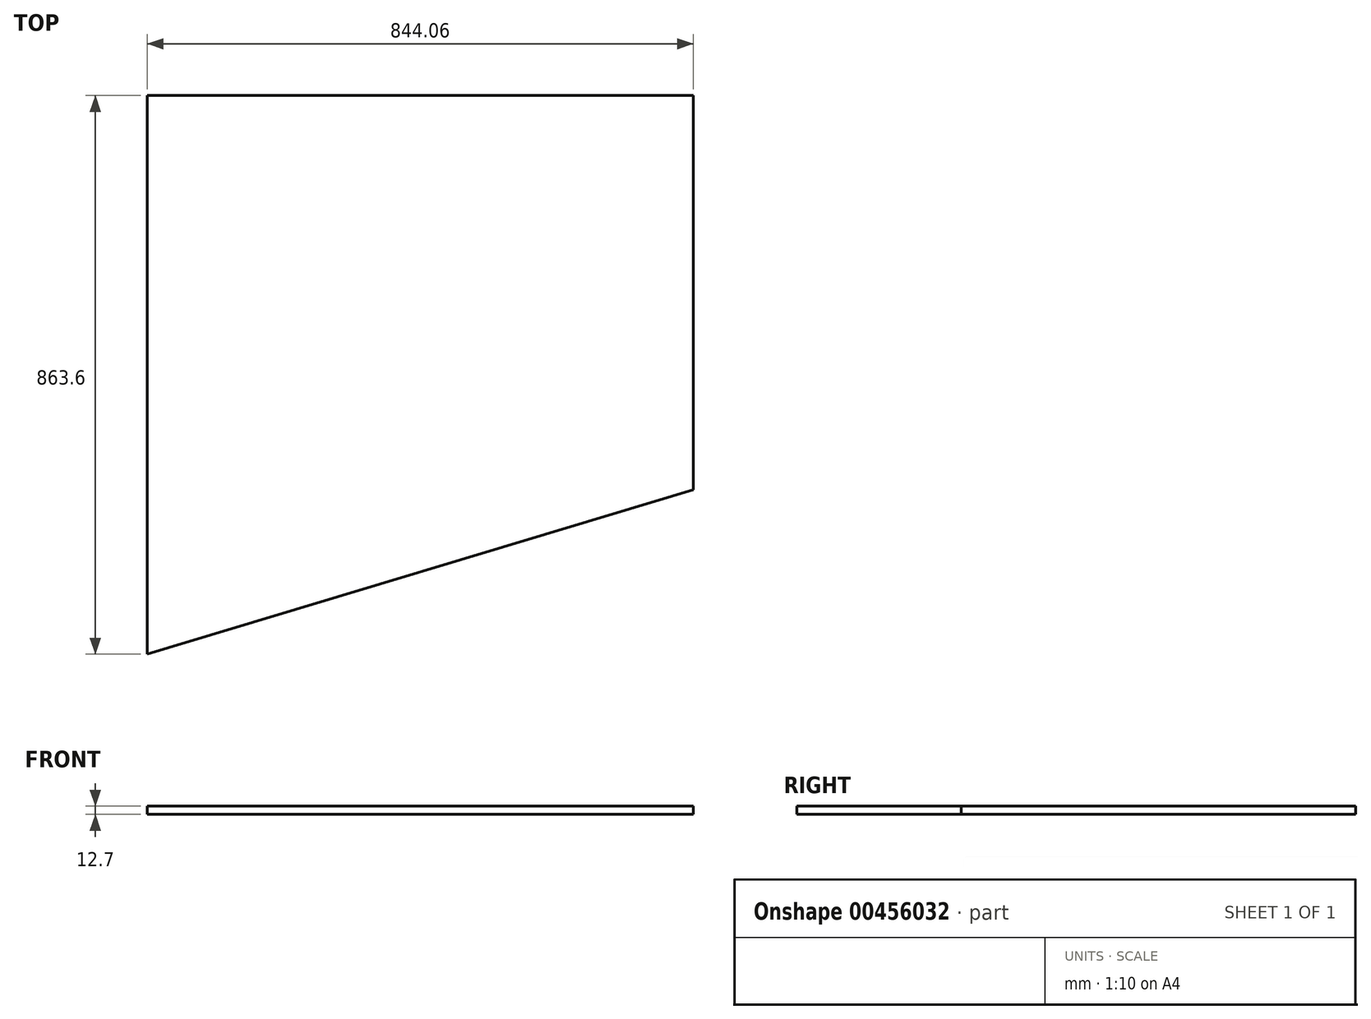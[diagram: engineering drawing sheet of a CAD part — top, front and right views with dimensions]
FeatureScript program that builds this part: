
annotation { "Feature Type Name" : "Feature", "Feature Type Description" : "" }
export const myFeature = defineFeature(function(context is Context, id is Id, definition is map)
    precondition{}
    {
        {
            var Q0;
            Q0=qCreatedBy(makeId("Top.planeOp"),FACE);
            var sketch = newSketch(context, id + "F0", { "sketchPlane" : qUnion([Q0])});
            skLineSegment(sketch, "E0.bottom", {"start": v(0, 0) * mm, "end": v(844.06, 0) * mm});
            skLineSegment(sketch, "E0.left", {"start": v(0, 0) * mm, "end": v(0, -863.6) * mm});
            skLineSegment(sketch, "E1", {"start": v(844.06, 0) * mm, "end": v(844.06, -609.6) * mm});
            skLineSegment(sketch, "E2", {"start": v(0, -863.6) * mm, "end": v(844.06, -609.6) * mm});
            skSolve(sketch);
        }
        {
            var Q0;
            Q0=makeQuery(id+"F0.imprint","IMPRINT",FACE,{"disambiguationData":[TD([[makeQuery(id+"F0.imprint","IMPRINT",EDGE,{"derivedFrom":sQuery(id+"F0.wireOp",EDGE,"E0.bottom")}),-1.0]])]});
            extrude(context, id + "F1", {"entities" : qUnion([Q0]), "depth" : 12.7 * mm});
        }
    });
